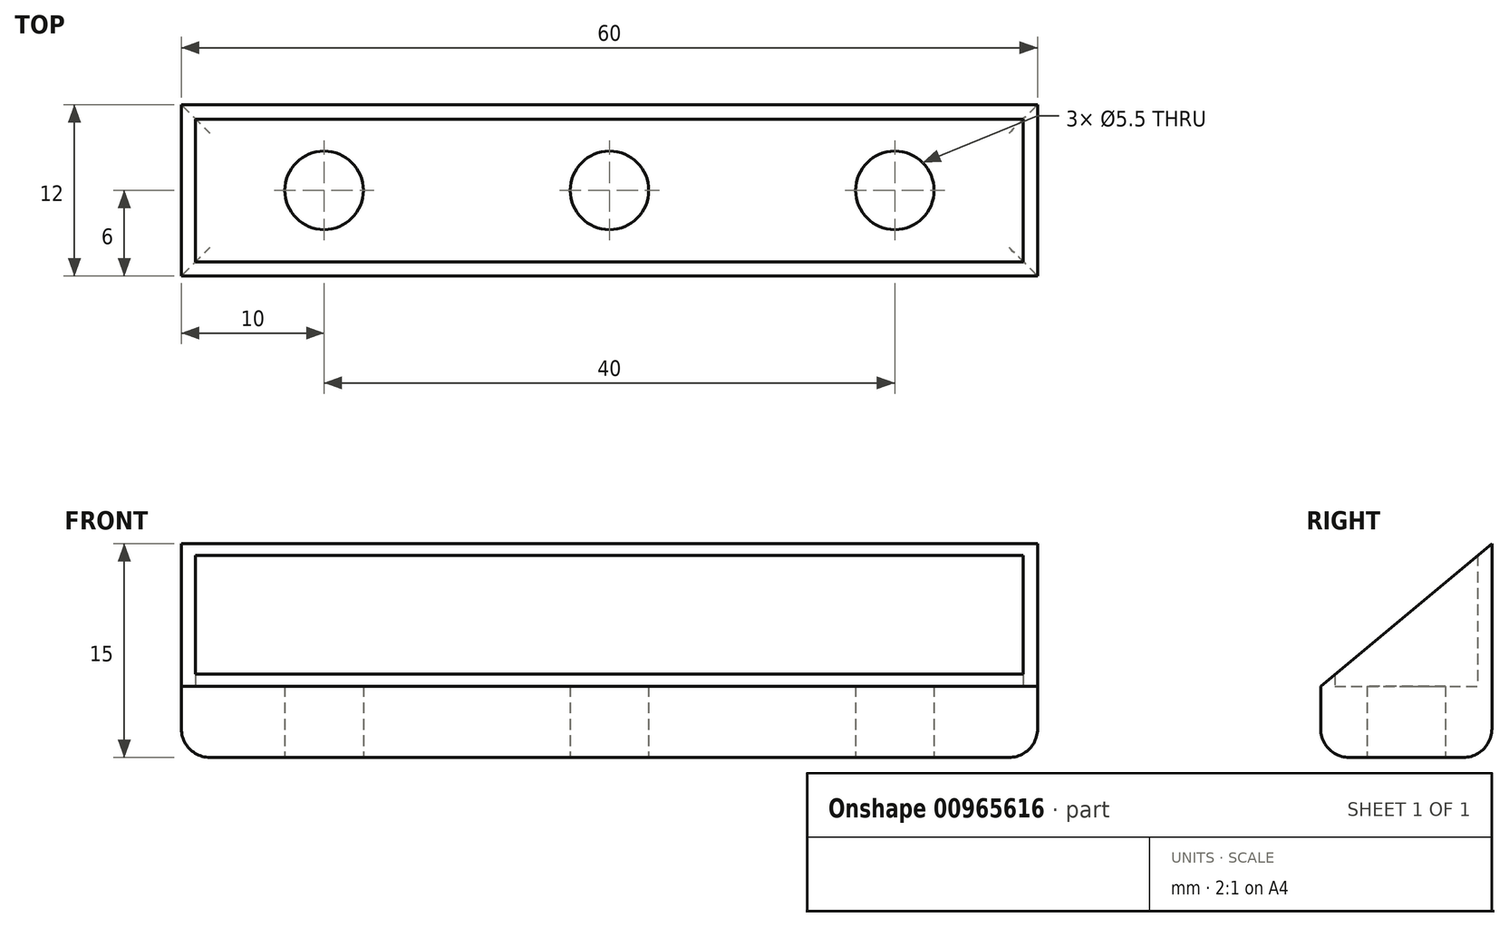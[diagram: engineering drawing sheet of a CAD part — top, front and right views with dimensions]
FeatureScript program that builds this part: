
annotation { "Feature Type Name" : "Feature", "Feature Type Description" : "" }
export const myFeature = defineFeature(function(context is Context, id is Id, definition is map)
    precondition{}
    {
        {
            var Q0;
            Q0=qCreatedBy(makeId("Top.planeOp"),FACE);
            var sketch = newSketch(context, id + "F0", { "sketchPlane" : qUnion([Q0])});
            skLineSegment(sketch, "E0.bottom", {"start": v(-30, 6) * mm, "end": v(30, 6) * mm});
            skLineSegment(sketch, "E0.top", {"start": v(-30, -6) * mm, "end": v(30, -6) * mm});
            skLineSegment(sketch, "E0.left", {"start": v(-30, 6) * mm, "end": v(-30, -6) * mm});
            skLineSegment(sketch, "E0.right", {"start": v(30, 6) * mm, "end": v(30, -6) * mm});
            skPoint(sketch, "E0.middle", {"position": v(0, 0) * mm});
            skCircle(sketch, "E1", {"center": v(-20, 0) * mm, "radius": 2.75 * mm});
            skCircle(sketch, "E2", {"center": v(0, 0) * mm, "radius": 2.75 * mm});
            skCircle(sketch, "E3", {"center": v(20, 0) * mm, "radius": 2.75 * mm});
            skLineSegment(sketch, "E4.bottom", {"start": v(-29, -5) * mm, "end": v(29, -5) * mm});
            skLineSegment(sketch, "E4.top", {"start": v(-29, 5) * mm, "end": v(29, 5) * mm});
            skLineSegment(sketch, "E4.left", {"start": v(-29, -5) * mm, "end": v(-29, 5) * mm});
            skLineSegment(sketch, "E4.right", {"start": v(29, -5) * mm, "end": v(29, 5) * mm});
            skSolve(sketch);
        }
        {
            var Q0;
            Q0=makeQuery(id+"F0.imprint","IMPRINT",FACE,{"disambiguationData":[TD([[makeQuery(id+"F0.imprint","IMPRINT",EDGE,{"derivedFrom":sQuery(id+"F0.wireOp",EDGE,"E0.bottom")}),-1.0]])]});
            var Q1;
            Q1=makeQuery(id+"F0.imprint","IMPRINT",FACE,{"disambiguationData":[TD([[makeQuery(id+"F0.imprint","IMPRINT",EDGE,{"derivedFrom":sQuery(id+"F0.wireOp",EDGE,"E1")}),-1.0]])]});
            extrude(context, id + "F1", {"entities" : qUnion([Q0, Q1]), "depth" : 5 * mm, "offsetDistance" : 25 * mm});
        }
        {
            var Q0;
            Q0=qCreatedBy(makeId("Right.planeOp"),FACE);
            var sketch = newSketch(context, id + "F2", { "sketchPlane" : qUnion([Q0])});
            skLineSegment(sketch, "E5", {"start": v(-6, 5) * mm, "end": v(6, 15) * mm});
            skLineSegment(sketch, "E6", {"start": v(6, 15) * mm, "end": v(6, 5) * mm});
            skLineSegment(sketch, "E7", {"start": v(6, 5) * mm, "end": v(-6, 5) * mm});
            skSolve(sketch);
        }
        {
            var Q0;
            Q0=makeQuery(id+"F2.imprint","IMPRINT",FACE,{"disambiguationData":[TD([[makeQuery(id+"F2.imprint","IMPRINT",EDGE,{"derivedFrom":sQuery(id+"F2.wireOp",EDGE,"E5")}),-1.0]])]});
            var Q1;
            Q1=makeQuery(id+"F1.opExtrude","SWEPT_FACE",FACE,{"disambiguationData":[OSD([sQuery(id+"F0.wireOp",EDGE,"E0.left")])]});
            var Q2;
            Q2=makeQuery(id+"F1.opExtrude","SWEPT_FACE",FACE,{"disambiguationData":[OSD([sQuery(id+"F0.wireOp",EDGE,"E0.right")])]});
            extrude(context, id + "F3", {"entities" : qUnion([Q0]), "operationType" : NewBodyOperationType.ADD, "endBound" : BoundingType.UP_TO_SURFACE, "oppositeDirection" : true, "depth" : 25 * mm, "endBoundEntityFace" : qUnion([Q1]), "offsetDistance" : 25 * mm, "hasSecondDirection" : true, "secondDirectionBound" : SecondDirectionBoundingType.UP_TO_SURFACE, "secondDirectionOppositeDirection" : false, "secondDirectionDepth" : 25 * mm, "secondDirectionBoundEntityFace" : qUnion([Q2])});
        }
        {
            var Q0;
            Q0=makeQuery(id+"F0.imprint","IMPRINT",FACE,{"disambiguationData":[TD([[makeQuery(id+"F0.imprint","IMPRINT",EDGE,{"derivedFrom":sQuery(id+"F0.wireOp",EDGE,"E1")}),-1.0]])]});
            var Q1;
            Q1=makeQuery(id+"F0.imprint","IMPRINT",FACE,{"disambiguationData":[TD([[makeQuery(id+"F0.imprint","IMPRINT",EDGE,{"derivedFrom":sQuery(id+"F0.wireOp",EDGE,"E2")}),1.0]])]});
            var Q2;
            Q2=makeQuery(id+"F0.imprint","IMPRINT",FACE,{"disambiguationData":[TD([[makeQuery(id+"F0.imprint","IMPRINT",EDGE,{"derivedFrom":sQuery(id+"F0.wireOp",EDGE,"E1")}),1.0]])]});
            var Q3;
            Q3=makeQuery(id+"F0.imprint","IMPRINT",FACE,{"disambiguationData":[TD([[makeQuery(id+"F0.imprint","IMPRINT",EDGE,{"derivedFrom":sQuery(id+"F0.wireOp",EDGE,"E3")}),1.0]])]});
            extrude(context, id + "F4", {"entities" : qUnion([Q0, Q1, Q2, Q3]), "operationType" : NewBodyOperationType.REMOVE, "endBound" : BoundingType.THROUGH_ALL, "depth" : 25 * mm, "offsetDistance" : 25 * mm, "hasSecondDirection" : true, "secondDirectionOppositeDirection" : false, "secondDirectionDepth" : 5 * mm});
        }
        {
            var Q0;
            Q0=makeQuery(id+"F1.opExtrude","CAP_EDGE",EDGE,{"disambiguationData":[OSD([sQuery(id+"F0.wireOp",EDGE,"E0.bottom")])],"isStart":true});
            var Q1;
            Q1=makeQuery(id+"F1.opExtrude","CAP_EDGE",EDGE,{"disambiguationData":[OSD([sQuery(id+"F0.wireOp",EDGE,"E0.right")])],"isStart":true});
            var Q2;
            Q2=makeQuery(id+"F1.opExtrude","CAP_EDGE",EDGE,{"disambiguationData":[OSD([sQuery(id+"F0.wireOp",EDGE,"E0.top")])],"isStart":true});
            var Q3;
            Q3=makeQuery(id+"F1.opExtrude","CAP_EDGE",EDGE,{"disambiguationData":[OSD([sQuery(id+"F0.wireOp",EDGE,"E0.left")])],"isStart":true});
            fillet(context, id + "F5", {"entities" : qUnion([Q0, Q1, Q2, Q3]), "radius" : 2 * mm, "tangentPropagation" : true, "allowEdgeOverflow" : false});
        }
    });
